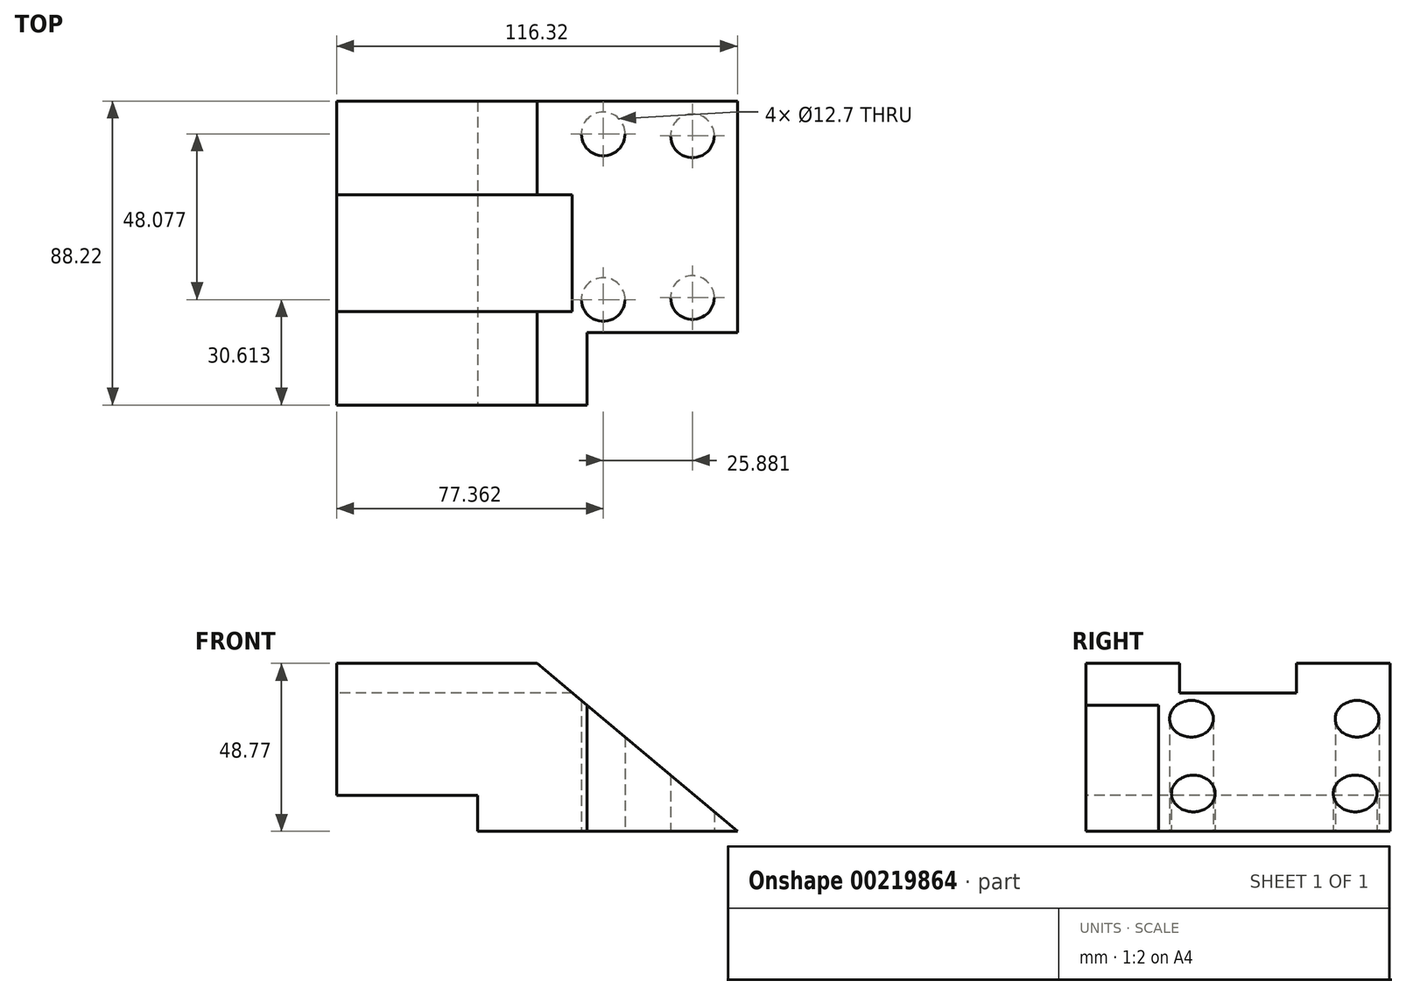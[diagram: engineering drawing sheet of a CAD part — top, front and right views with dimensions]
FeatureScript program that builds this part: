
annotation { "Feature Type Name" : "Feature", "Feature Type Description" : "" }
export const myFeature = defineFeature(function(context is Context, id is Id, definition is map)
    precondition{}
    {
        {
            var Q0;
            Q0=qCreatedBy(makeId("Top.planeOp"),FACE);
            var sketch = newSketch(context, id + "F0", { "sketchPlane" : qUnion([Q0])});
            skLineSegment(sketch, "E0.bottom", {"start": v(58.16, 44.1) * mm, "end": v(-58.16, 44.1) * mm});
            skLineSegment(sketch, "E0.top", {"start": v(58.16, -44.1) * mm, "end": v(-58.16, -44.1) * mm});
            skLineSegment(sketch, "E0.left", {"start": v(58.16, 44.1) * mm, "end": v(58.16, -44.1) * mm});
            skLineSegment(sketch, "E0.right", {"start": v(-58.16, 44.1) * mm, "end": v(-58.16, -44.1) * mm});
            skPoint(sketch, "E0.middle", {"position": v(0, 0) * mm});
            skSolve(sketch);
        }
        {
            var Q0;
            Q0=makeQuery(id+"F0.imprint","IMPRINT",FACE,{"disambiguationData":[TD([[makeQuery(id+"F0.imprint","IMPRINT",EDGE,{"derivedFrom":sQuery(id+"F0.wireOp",EDGE,"E0.bottom")}),1.0]])]});
            extrude(context, id + "F1", {"entities" : qUnion([Q0]), "depth" : 48.77 * mm});
        }
        {
            var Q0;
            Q0=makeQuery(id+"F1.opExtrude","SWEPT_FACE",FACE,{"disambiguationData":[OSD([sQuery(id+"F0.wireOp",EDGE,"E0.top")])]});
            var sketch = newSketch(context, id + "F2", { "sketchPlane" : qUnion([Q0])});
            skLineSegment(sketch, "E1", {"start": v(58.16, 48.77) * mm, "end": v(0, 48.77) * mm});
            skLineSegment(sketch, "E2", {"start": v(0, 48.77) * mm, "end": v(58.16, 0) * mm});
            skLineSegment(sketch, "E3", {"start": v(58.16, 0) * mm, "end": v(58.16, 48.77) * mm});
            skLineSegment(sketch, "E4", {"start": v(0, 48.77) * mm, "end": v(0, 0) * mm});
            skLineSegment(sketch, "E5", {"start": v(0, 0) * mm, "end": v(58.16, 0) * mm});
            skSolve(sketch);
        }
        {
            var Q0;
            Q0=makeQuery(id+"F2.imprint","IMPRINT",FACE,{"disambiguationData":[TD([[makeQuery(id+"F2.imprint","IMPRINT",EDGE,{"derivedFrom":sQuery(id+"F2.wireOp",EDGE,"E1")}),1.0]])]});
            extrude(context, id + "F3", {"entities" : qUnion([Q0]), "operationType" : NewBodyOperationType.REMOVE, "oppositeDirection" : true, "depth" : 93.22 * mm});
        }
        {
            var Q0;
            Q0=makeQuery(id+"F1.opExtrude","SWEPT_FACE",FACE,{"disambiguationData":[OSD([sQuery(id+"F0.wireOp",EDGE,"E0.top")])]});
            var sketch = newSketch(context, id + "F4", { "sketchPlane" : qUnion([Q0])});
            skLineSegment(sketch, "E6", {"start": v(14.46, 36.64) * mm, "end": v(14.46, 0) * mm});
            skLineSegment(sketch, "E7", {"start": v(14.46, 0) * mm, "end": v(58.16, 0) * mm});
            skLineSegment(sketch, "E8", {"start": v(58.16, 0) * mm, "end": v(14.46, 36.64) * mm});
            skSolve(sketch);
        }
        {
            var Q0;
            Q0 = qSketchRegion(id + "F4", true);
            extrude(context, id + "F5", {"entities" : qUnion([Q0]), "operationType" : NewBodyOperationType.REMOVE, "oppositeDirection" : true, "depth" : 21.08 * mm});
        }
        {
            var Q0;
            Q0=makeQuery(id+"F1.opExtrude","SWEPT_FACE",FACE,{"disambiguationData":[OSD([sQuery(id+"F0.wireOp",EDGE,"E0.top")])]});
            var sketch = newSketch(context, id + "F6", { "sketchPlane" : qUnion([Q0])});
            skLineSegment(sketch, "E9", {"start": v(-58.16, 0) * mm, "end": v(-58.16, 10.44) * mm});
            skLineSegment(sketch, "E10", {"start": v(-58.16, 10.44) * mm, "end": v(-17.25, 10.44) * mm});
            skLineSegment(sketch, "E11", {"start": v(-17.25, 10.44) * mm, "end": v(-17.25, 0) * mm});
            skLineSegment(sketch, "E12", {"start": v(-17.25, 0) * mm, "end": v(-58.16, 0) * mm});
            skSolve(sketch);
        }
        {
            var Q0;
            Q0 = qSketchRegion(id + "F6", true);
            extrude(context, id + "F7", {"entities" : qUnion([Q0]), "operationType" : NewBodyOperationType.REMOVE, "oppositeDirection" : true, "depth" : 91.7 * mm});
        }
        {
            var Q0;
            Q0=makeQuery(id+"F1.opExtrude","SWEPT_FACE",FACE,{"disambiguationData":[OSD([sQuery(id+"F0.wireOp",EDGE,"E0.right")])]});
            var sketch = newSketch(context, id + "F8", { "sketchPlane" : qUnion([Q0])});
            skLineSegment(sketch, "E13.bottom", {"start": v(16.98, 40.21) * mm, "end": v(-16.98, 40.21) * mm});
            skLineSegment(sketch, "E13.top", {"start": v(16.98, 57.32) * mm, "end": v(-16.98, 57.32) * mm});
            skLineSegment(sketch, "E13.left", {"start": v(16.98, 40.21) * mm, "end": v(16.98, 57.32) * mm});
            skLineSegment(sketch, "E13.right", {"start": v(-16.98, 40.21) * mm, "end": v(-16.98, 57.32) * mm});
            skPoint(sketch, "E13.middle", {"position": v(0, 48.77) * mm});
            skSolve(sketch);
        }
        {
            var Q0;
            Q0 = qSketchRegion(id + "F8", true);
            extrude(context, id + "F9", {"entities" : qUnion([Q0]), "operationType" : NewBodyOperationType.REMOVE, "oppositeDirection" : true, "depth" : 78.49 * mm});
        }
        {
            var Q0;
            Q0=makeQuery(id+"F1.opExtrude","CAP_FACE",FACE,{"disambiguationData":[OSD([sQuery(id+"F0.wireOp",EDGE,"E0.bottom"),sQuery(id+"F0.wireOp",EDGE,"E0.top"),sQuery(id+"F0.wireOp",EDGE,"E0.left"),sQuery(id+"F0.wireOp",EDGE,"E0.right")])],"isStart":true});
            var sketch = newSketch(context, id + "F10", { "sketchPlane" : qUnion([Q0])});
            skCircle(sketch, "E14", {"center": v(45.08, 12.94) * mm, "radius": 6.35 * mm});
            skCircle(sketch, "E15", {"center": v(19.2, 13.5) * mm, "radius": 6.35 * mm});
            skCircle(sketch, "E16.MirrorC", {"center": v(45.08, -34.02) * mm, "radius": 6.35 * mm});
            skCircle(sketch, "E17.MirrorC", {"center": v(19.2, -34.58) * mm, "radius": 6.35 * mm});
            skPoint(sketch, "E18.start.orphan", {"position": v(58.16, -10.54) * mm});
            skSolve(sketch);
        }
        {
            var Q0;
            Q0 = qSketchRegion(id + "F10", true);
            extrude(context, id + "F11", {"entities" : qUnion([Q0]), "operationType" : NewBodyOperationType.REMOVE, "oppositeDirection" : true, "depth" : 58.93 * mm});
        }
    });
